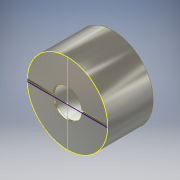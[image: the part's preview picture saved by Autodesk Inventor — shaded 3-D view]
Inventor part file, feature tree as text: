
AUTODESK INVENTOR PART (.ipt)
format: ipt  version: 2018 (Build 220112000, 112)  size: 141,824 bytes
history: native  units: in
note: dims shown in document units (in); Inventor stores cm internally (conversion verified against a paired STEP export)
features: extrude x4, sketch x2, shell x1
ambient origin geometry x8: Origin, YZ Plane, XZ Plane, XY Plane, X Axis, Y Axis, Z Axis, Center Point
bodies: Solid1 (feature_tree)
feature tree (7):
  sketch  "Sketch1"  dims[d0=0.65in d1=0.369in d2=0.0in d3=0.015in]
  extrude  "Extrusion1"  Depth=0.369in TaperAngle=0.0deg
  shell  "Shell1"  Thickness=0.015in
  extrude  "Extrusion3"  Depth=0.02in
  extrude  "Extrusion4"  Depth=0.02in TaperAngle=0.0deg
  extrude  "Extrusion5"  Depth=0.02in TaperAngle=0.0deg
  sketch  "Sketch2"  dims[d13=0.235in d14=0.02in d17=0.69in d18=0.0in d19=0.69in d20=0.0in d21=0.69in d22=0.0in]
